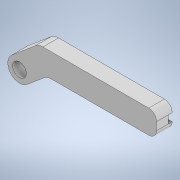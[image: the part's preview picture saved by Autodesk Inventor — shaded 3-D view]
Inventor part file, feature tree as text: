
AUTODESK INVENTOR PART (.ipt)
format: ipt  version: 2020 (Build 240168000, 168)  size: 128,000 bytes
history: native  units: mm
features: extrude x2, sketch x2
ambient origin geometry x8: Origin, YZ Plane, XZ Plane, XY Plane, X Axis, Y Axis, Z Axis, Center Point
bodies: Solid1 (feature_tree)
feature tree (4):
  extrude  "Extrusion1"  Depth=6.0mm
  extrude  "Extrusion3"  Depth=1.0mm
  sketch  "Sketch1"  dims[d0=6.0mm d1=6.0mm]
  sketch  "Sketch3"  dims[d2=3.0mm d3=24.43461mm d4=2.0mm d5=2.0mm d6=35.0mm d7=3.5mm d8=4.0mm d9=0.0mm d14=28.0mm d15=2.0mm d16=1.0mm d17=0.0mm]
